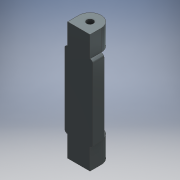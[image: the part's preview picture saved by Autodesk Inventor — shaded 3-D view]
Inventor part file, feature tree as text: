
AUTODESK INVENTOR PART (.ipt)
format: ipt  version: 2016 (Build 200138000, 138)  size: 188,416 bytes
history: native  units: mm
features: extrude x7, sketch x7, chamfer x2, fillet x1
ambient origin geometry x8: Origin, YZ Plane, XZ Plane, XY Plane, X Axis, Y Axis, Z Axis, Center Point
bodies: Solid1 (feature_tree)
feature tree (17):
  extrude  "Extrusion1"  Depth=8.5mm
  extrude  "Extrusion2"  Depth=2.0mm
  extrude  "Extrusion3"  Depth=1.1mm
  extrude  "Extrusion4"  Depth=1.1mm
  extrude  "Extrusion6"  Depth=10.0mm TaperAngle=0.0deg
  extrude  "Extrusion7"  Depth=10.0mm
  extrude  "Extrusion8"  Depth=10.0mm TaperAngle=0.0deg
  chamfer  "Chamfer1"  Distance=10.0mm
  chamfer  "Chamfer2"  Distance=10.0mm
  fillet  "Fillet1"  Radius=2.0mm
  sketch  "Sketch1"  dims[d7=8.5mm d8=8.5mm]
  sketch  "Sketch4"  dims[d9=2.0mm d10=2.0mm]
  sketch  "Sketch5"  dims[d11=10.7mm d12=1.1mm]
  sketch  "Sketch6"  dims[d13=1.1mm d14=29.0mm]
  sketch  "Sketch9"  dims[d15=4.25mm d16=0.0mm d20=10.0mm d21=0.0mm]
  sketch  "Sketch10"  dims[d22=10.0mm d23=0.0mm d24=2.5mm]
  sketch  "Sketch11"  dims[d25=10.0mm d26=0.0mm d29=10.0mm d30=0.0mm d31=10.0mm d32=0.0mm d33=10.0mm d34=0.0mm d37=2.0mm d38=2.0mm d39=45.0deg d40=2.0mm d41=2.0mm d42=45.0deg d43=1.1mm]
